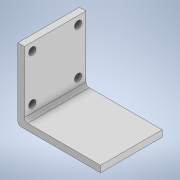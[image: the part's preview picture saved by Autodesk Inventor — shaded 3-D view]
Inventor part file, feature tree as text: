
AUTODESK INVENTOR PART (.ipt)
format: ipt  version: 2021 (Build 250183000, 183)  size: 119,808 bytes
history: native  units: mm
features: sketch x2, extrude x1, hole x1, projected_geometry x1
ambient origin geometry x8: Origin, YZ Plane, XZ Plane, XY Plane, X Axis, Y Axis, Z Axis, Center Point
bodies: Solid1 (feature_tree)
feature tree (5):
  extrude  "Extrusion1"  Depth=4.0mm
  hole  "Hole1"  [1 undecoded]
  sketch  "Sketch1"  dims[d0=2.0mm d1=4.0mm]
  sketch  "Sketch2"  dims[d2=4.0mm d3=38.0mm d5=45.0mm d6=38.0mm d7=0.0mm d8=28.284mm d9=28.284mm d10=4.5mm d11=6.0mm d12=8.0mm d13=4.0mm d14=90.0deg d15=8.0mm d16=20.594885mm]
  projected_geometry  "Projected Loop1"
note: 1 required parameter value undecoded (feature->parameter linkage not recoverable at this tier; creation-order binding heuristic only, values carry confidence <= 0.55)
